# Revit family: TCC
name_source: partatom
category: Air Terminals
revit_build: Autodesk Revit MEP 2012 (Build: 20110309_2315(x64)
units: mm (PartAtom-declared; Revit-internal decimal feet)

## types (4) — shared parameters
Manufacturer = INNES
Máxima presión estática = 0.00 in-wg
Máxima velocidad de cuello = 0 FPM
Mínima presión estática = 0.00 in-wg
Mínima velocidad de cuello = 0 FPM
Separacion = 31/64"
Separacion vertical = 3/4"
URL = http://www.innes.com.mx

## per-type parameters (varying)
| type | A | B | Horizontal | Largo aleta | Largo rejilla | No. de elementos horizontales | No. de elementos vertical | Vertical | a | b |
| TCC-10-7 | 8 7/16" | 11 7/16" | 10" | 8 29/32" | 6 3/32" | 13 | 12 | 7" | 6 7/16" | 9 7/16" |
| TCC-20-10 | 11 7/16" | 21 7/16" | 20" | 18 29/32" | 9 3/32" | 19 | 25 | 10" | 9 7/16" | 19 7/16" |
| TCC-120-12 | 13 7/16" | 121 7/16" | 120" | 118 29/32" | 11 3/32" | 23 | 159 | 12" | 11 7/16" | 119 7/16" |
| TCC-30-27 | 28 7/16" | 31 7/16" | 30" | 28 29/32" | 26 3/32" | 54 | 39 | 27" | 26 7/16" | 29 7/16" |

## geometry (parser evidence)
native form markers: Sweep x4
no freeform markers — native parametric forms only
